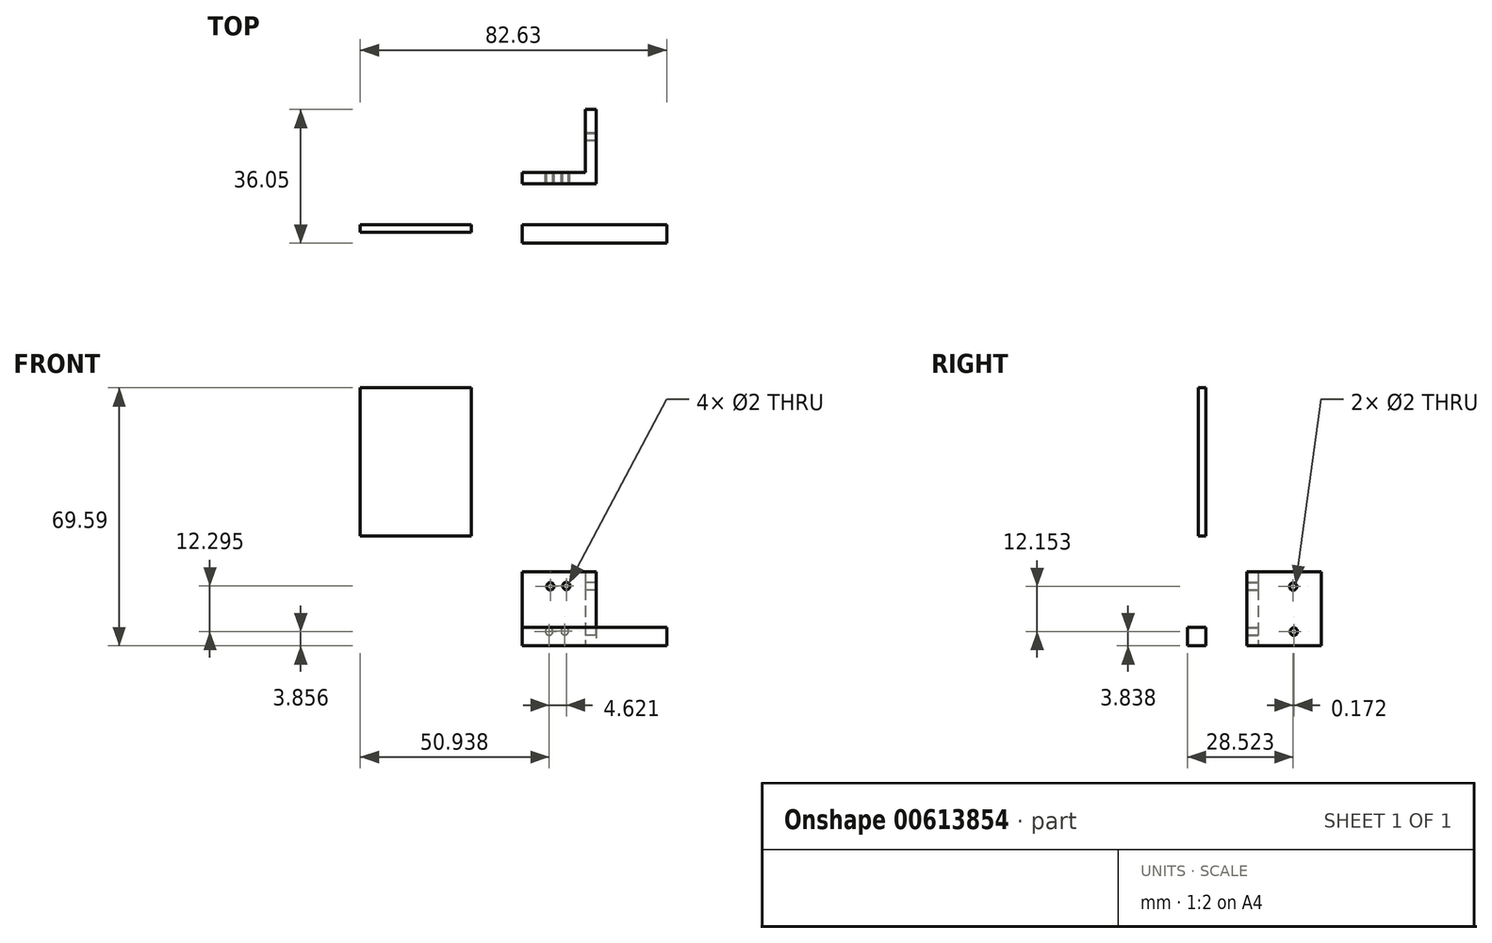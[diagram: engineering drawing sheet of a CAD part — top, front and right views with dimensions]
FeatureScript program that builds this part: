
annotation { "Feature Type Name" : "Feature", "Feature Type Description" : "" }
export const myFeature = defineFeature(function(context is Context, id is Id, definition is map)
    precondition{}
    {
        {
            var Q0;
            Q0=qCreatedBy(makeId("Front.planeOp"),FACE);
            var sketch = newSketch(context, id + "F0", { "sketchPlane" : qUnion([Q0])});
            skLineSegment(sketch, "E0.bottom", {"start": v(0, 5) * mm, "end": v(39, 5) * mm});
            skLineSegment(sketch, "E0.top", {"start": v(0, 0) * mm, "end": v(39, 0) * mm});
            skLineSegment(sketch, "E0.left", {"start": v(0, 5) * mm, "end": v(0, 0) * mm});
            skLineSegment(sketch, "E0.right", {"start": v(39, 5) * mm, "end": v(39, 0) * mm});
            skSolve(sketch);
        }
        {
            var Q0;
            Q0=makeQuery(id+"F0.imprint","IMPRINT",FACE,{"disambiguationData":[TD([[makeQuery(id+"F0.imprint","IMPRINT",EDGE,{"derivedFrom":sQuery(id+"F0.wireOp",EDGE,"E0.bottom")}),-1.0]])]});
            extrude(context, id + "F1", {"entities" : qUnion([Q0]), "depth" : 5 * mm, "offsetDistance" : 25 * mm});
        }
        {
            var Q0;
            Q0=qCreatedBy(makeId("Front.planeOp"),FACE);
            var sketch = newSketch(context, id + "F2", { "sketchPlane" : qUnion([Q0])});
            skLineSegment(sketch, "E1.bottom", {"start": v(-43.63, 69.6) * mm, "end": v(-13.63, 69.6) * mm});
            skLineSegment(sketch, "E1.top", {"start": v(-43.63, 29.6) * mm, "end": v(-13.63, 29.6) * mm});
            skLineSegment(sketch, "E1.left", {"start": v(-43.63, 69.6) * mm, "end": v(-43.63, 29.6) * mm});
            skLineSegment(sketch, "E1.right", {"start": v(-13.63, 69.6) * mm, "end": v(-13.63, 29.6) * mm});
            skSolve(sketch);
        }
        {
            var Q0;
            Q0=makeQuery(id+"F2.imprint","IMPRINT",FACE,{"disambiguationData":[TD([[makeQuery(id+"F2.imprint","IMPRINT",EDGE,{"derivedFrom":sQuery(id+"F2.wireOp",EDGE,"E1.bottom")}),-1.0]])]});
            extrude(context, id + "F3", {"entities" : qUnion([Q0]), "depth" : 2 * mm, "offsetDistance" : 25 * mm});
        }
        {
            var Q0;
            Q0=qCreatedBy(makeId("Top.planeOp"),FACE);
            var sketch = newSketch(context, id + "F4", { "sketchPlane" : qUnion([Q0])});
            skLineSegment(sketch, "E2", {"start": v(0, 14.05) * mm, "end": v(17, 14.05) * mm});
            skLineSegment(sketch, "E3", {"start": v(17, 14.05) * mm, "end": v(17, 31.05) * mm});
            skLineSegment(sketch, "E4", {"start": v(17, 31.05) * mm, "end": v(20, 31.05) * mm});
            skLineSegment(sketch, "E5", {"start": v(20, 31.05) * mm, "end": v(20, 11.05) * mm});
            skLineSegment(sketch, "E6", {"start": v(20, 11.05) * mm, "end": v(0, 11.05) * mm});
            skLineSegment(sketch, "E7", {"start": v(0, 11.05) * mm, "end": v(0, 14.05) * mm});
            skSolve(sketch);
        }
        {
            var Q0;
            Q0=makeQuery(id+"F4.imprint","IMPRINT",FACE,{"disambiguationData":[TD([[makeQuery(id+"F4.imprint","IMPRINT",EDGE,{"derivedFrom":sQuery(id+"F4.wireOp",EDGE,"E2")}),-1.0]])]});
            extrude(context, id + "F5", {"entities" : qUnion([Q0]), "depth" : 20 * mm, "offsetDistance" : 25 * mm});
        }
        {
            var Q0;
            Q0=makeQuery(id+"F5.opExtrude","SWEPT_FACE",FACE,{"disambiguationData":[OSD([sQuery(id+"F4.wireOp",EDGE,"E3")])]});
            var sketch = newSketch(context, id + "F6", { "sketchPlane" : qUnion([Q0])});
            skPoint(sketch, "E8", {"position": v(-23.7, 3.84) * mm});
            skPoint(sketch, "E9", {"position": v(-23.52, 16) * mm});
            skSolve(sketch);
        }
        {
            var Q0;
            Q0=makeQuery(id+"F5.opExtrude","SWEPT_FACE",FACE,{"disambiguationData":[OSD([sQuery(id+"F4.wireOp",EDGE,"E2")])]});
            var sketch = newSketch(context, id + "F7", { "sketchPlane" : qUnion([Q0])});
            skPoint(sketch, "E10", {"position": v(-7.3, 3.86) * mm});
            skPoint(sketch, "E11", {"position": v(-7.62, 16.04) * mm});
            skPoint(sketch, "E12", {"position": v(-11.52, 3.95) * mm});
            skPoint(sketch, "E13", {"position": v(-11.93, 16.15) * mm});
            skSolve(sketch);
        }
        {
            var Q0;
            Q0=sQuery(id+"F7.wireOp",VERTEX,"E10");
            var Q1;
            Q1=sQuery(id+"F7.wireOp",VERTEX,"E12");
            var Q2;
            Q2=sQuery(id+"F7.wireOp",VERTEX,"E13");
            var Q3;
            Q3=sQuery(id+"F7.wireOp",VERTEX,"E11");
            var Q4;
            Q4=sQuery(id+"F6.wireOp",VERTEX,"E9");
            var Q5;
            Q5=sQuery(id+"F6.wireOp",VERTEX,"E8");
            var Q6;
            Q6=makeQuery(id+"F1.opExtrude","SWEPT_BODY",BODY,{"disambiguationData":[OSD([sQuery(id+"F0.wireOp",EDGE,"E0.bottom"),sQuery(id+"F0.wireOp",EDGE,"E0.top"),sQuery(id+"F0.wireOp",EDGE,"E0.left"),sQuery(id+"F0.wireOp",EDGE,"E0.right")])]});
            var Q7;
            Q7=makeQuery(id+"F5.opExtrude","SWEPT_BODY",BODY,{"disambiguationData":[OSD([sQuery(id+"F4.wireOp",EDGE,"E2"),sQuery(id+"F4.wireOp",EDGE,"E3"),sQuery(id+"F4.wireOp",EDGE,"E4"),sQuery(id+"F4.wireOp",EDGE,"E5"),sQuery(id+"F4.wireOp",EDGE,"E6"),sQuery(id+"F4.wireOp",EDGE,"E7")])]});
            hole(context, id + "F8", {"style" : HoleStyle.SIMPLE, "endStyle" : HoleEndStyle.BLIND, "holeDiameter" : 2 * mm, "majorDiameter" : 5 * mm, "holeDepth" : 5 * mm, "isTappedThrough" : true, "tappedDepth" : 12 * mm, "tapClearance" : 3, "startFromSketch" : true, "locations" : qUnion([Q0, Q1, Q2, Q3, Q4, Q5]), "scope" : qUnion([Q6, Q7])});
        }
    });
